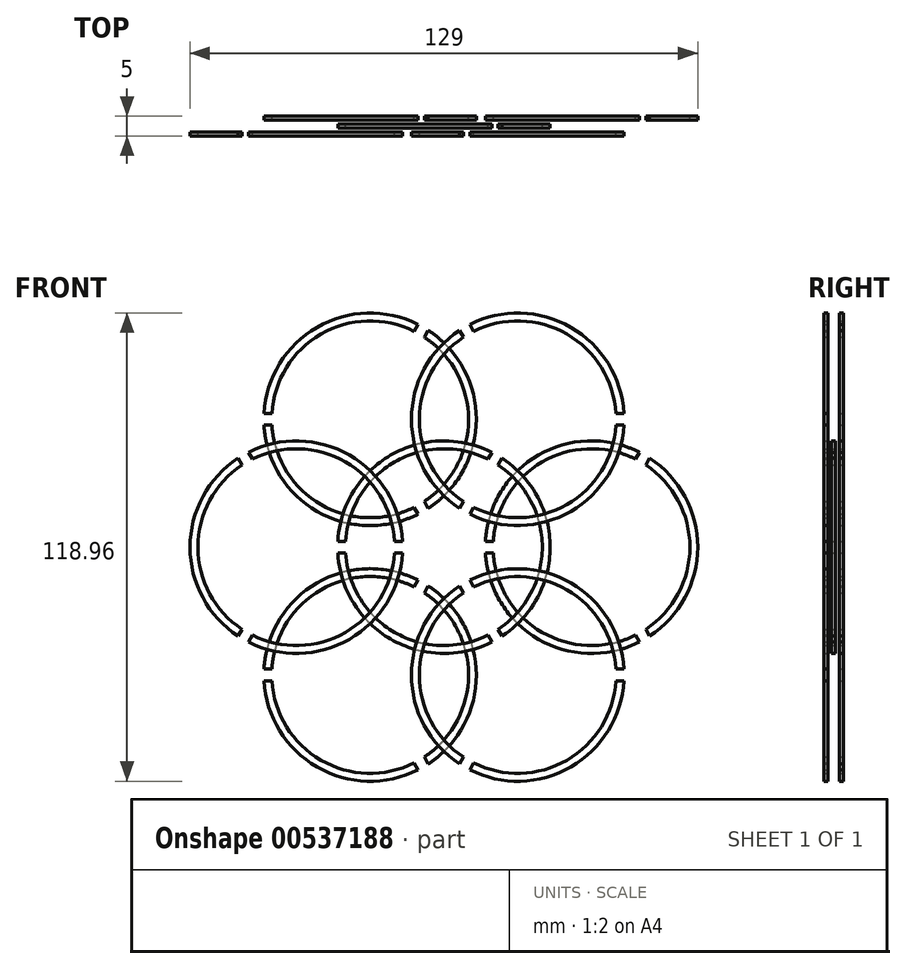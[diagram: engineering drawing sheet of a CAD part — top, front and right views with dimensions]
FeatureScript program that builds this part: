
annotation { "Feature Type Name" : "Feature", "Feature Type Description" : "" }
export const myFeature = defineFeature(function(context is Context, id is Id, definition is map)
    precondition{}
    {
        {
            var Q0;
            Q0=qCreatedBy(makeId("Front.planeOp"),FACE);
            var sketch = newSketch(context, id + "F0", { "sketchPlane" : qUnion([Q0])});
            skCircle(sketch, "E0", {"center": v(0, 0) * mm, "radius": 25 * mm});
            skCircle(sketch, "E1", {"center": v(0, 0) * mm, "radius": 27 * mm});
            skLineSegment(sketch, "E2", {"start": v(0, 0) * mm, "end": v(37.5, 0) * mm});
            skSolve(sketch);
        }
        {
            var Q0;
            Q0=qCreatedBy(makeId("Right.planeOp"),FACE);
            var sketch = newSketch(context, id + "F1", { "sketchPlane" : qUnion([Q0])});
            skLineSegment(sketch, "E3", {"start": v(-11.65, 0) * mm, "end": v(13.33, 0) * mm});
            skSolve(sketch);
        }
        {
            var Q0;
            Q0=makeQuery(id+"F0.imprint","IMPRINT",FACE,{"disambiguationData":[TD([[makeQuery(id+"F0.imprint","IMPRINT",EDGE,{"derivedFrom":sQuery(id+"F0.wireOp",EDGE,"E0")}),-1.0]])]});
            extrude(context, id + "F2", {"entities" : qUnion([Q0]), "depth" : 1 * mm, "offsetDistance" : 25 * mm});
        }
        {
            var Q0;
            Q0=qCreatedBy(makeId("Top.planeOp"),FACE);
            var sketch = newSketch(context, id + "F3", { "sketchPlane" : qUnion([Q0])});
            skLineSegment(sketch, "E4.bottom", {"start": v(16.08, -5.47) * mm, "end": v(-28.7, -5.47) * mm});
            skLineSegment(sketch, "E4.top", {"start": v(16.08, 4.96) * mm, "end": v(-28.7, 4.96) * mm});
            skLineSegment(sketch, "E4.left", {"start": v(16.08, -5.47) * mm, "end": v(16.08, 4.96) * mm});
            skLineSegment(sketch, "E4.right", {"start": v(-28.7, -5.47) * mm, "end": v(-28.7, 4.96) * mm});
            skSolve(sketch);
        }
        {
            var Q0;
            Q0=makeQuery(id+"F3.imprint","IMPRINT",FACE,{"disambiguationData":[TD([[makeQuery(id+"F3.imprint","IMPRINT",EDGE,{"derivedFrom":sQuery(id+"F3.wireOp",EDGE,"E4.bottom")}),-1.0]])]});
            extrude(context, id + "F4", {"entities" : qUnion([Q0]), "depth" : 3 * mm, "offsetDistance" : 25 * mm, "symmetric" : true});
        }
        {
            var Q0;
            Q0=makeQuery(id+"F4.opExtrude","SWEPT_BODY",BODY,{"disambiguationData":[OSD([sQuery(id+"F3.wireOp",EDGE,"E4.bottom"),sQuery(id+"F3.wireOp",EDGE,"E4.top"),sQuery(id+"F3.wireOp",EDGE,"E4.left"),sQuery(id+"F3.wireOp",EDGE,"E4.right")])]});
            var Q1;
            Q1=sQuery(id+"F1.wireOp",EDGE,"E3");
            circularPattern(context, id + "F5", {"entities" : qUnion([Q0]), "axis" : qUnion([Q1]), "angle" : 360 * degree, "instanceCount" : 3, "equalSpace" : true});
        }
        {
            var Q0;
            Q0=makeQuery(id+"F4.opExtrude","SWEPT_BODY",BODY,{"disambiguationData":[OSD([sQuery(id+"F3.wireOp",EDGE,"E4.bottom"),sQuery(id+"F3.wireOp",EDGE,"E4.top"),sQuery(id+"F3.wireOp",EDGE,"E4.left"),sQuery(id+"F3.wireOp",EDGE,"E4.right")])]});
            var Q1;
            Q1=makeQuery(id+"F5.opPattern","COPY",BODY,{"derivedFrom":makeQuery(id+"F4.opExtrude","SWEPT_BODY",BODY,{"disambiguationData":[OSD([sQuery(id+"F3.wireOp",EDGE,"E4.bottom"),sQuery(id+"F3.wireOp",EDGE,"E4.top"),sQuery(id+"F3.wireOp",EDGE,"E4.left"),sQuery(id+"F3.wireOp",EDGE,"E4.right")])]}),"instanceName":"2"});
            var Q2;
            Q2=makeQuery(id+"F5.opPattern","COPY",BODY,{"derivedFrom":makeQuery(id+"F4.opExtrude","SWEPT_BODY",BODY,{"disambiguationData":[OSD([sQuery(id+"F3.wireOp",EDGE,"E4.bottom"),sQuery(id+"F3.wireOp",EDGE,"E4.top"),sQuery(id+"F3.wireOp",EDGE,"E4.left"),sQuery(id+"F3.wireOp",EDGE,"E4.right")])]}),"instanceName":"1"});
            var Q3;
            Q3=makeQuery(id+"F2.opExtrude","SWEPT_BODY",BODY,{"disambiguationData":[OSD([sQuery(id+"F0.wireOp",EDGE,"E0"),sQuery(id+"F0.wireOp",EDGE,"E1")])]});
            var Q4;
            Q4=makeQuery(id+"F9.opPattern","COPY",BODY,{"derivedFrom":makeQuery(id+"F8.opPattern","COPY",BODY,{"derivedFrom":makeQuery(id+"F7.opPattern","COPY",BODY,{"derivedFrom":makeQuery(id+"F2.opExtrude","SWEPT_BODY",BODY,{"disambiguationData":[OSD([sQuery(id+"F0.wireOp",EDGE,"E0"),sQuery(id+"F0.wireOp",EDGE,"E1")])]}),"instanceName":"1"}),"instanceName":"1"}),"instanceName":"1"});
            var Q5;
            Q5=makeQuery(id+"F9.opPattern","COPY",BODY,{"derivedFrom":makeQuery(id+"F8.opPattern","COPY",BODY,{"derivedFrom":makeQuery(id+"F7.opPattern","COPY",BODY,{"derivedFrom":makeQuery(id+"F2.opExtrude","SWEPT_BODY",BODY,{"disambiguationData":[OSD([sQuery(id+"F0.wireOp",EDGE,"E0"),sQuery(id+"F0.wireOp",EDGE,"E1")])]}),"instanceName":"1"}),"instanceName":"2"}),"instanceName":"1"});
            var Q6;
            Q6=makeQuery(id+"F7.opPattern","COPY",BODY,{"derivedFrom":makeQuery(id+"F2.opExtrude","SWEPT_BODY",BODY,{"disambiguationData":[OSD([sQuery(id+"F0.wireOp",EDGE,"E0"),sQuery(id+"F0.wireOp",EDGE,"E1")])]}),"instanceName":"1"});
            var Q7;
            Q7=makeQuery(id+"F9.opPattern","COPY",BODY,{"derivedFrom":makeQuery(id+"F7.opPattern","COPY",BODY,{"derivedFrom":makeQuery(id+"F2.opExtrude","SWEPT_BODY",BODY,{"disambiguationData":[OSD([sQuery(id+"F0.wireOp",EDGE,"E0"),sQuery(id+"F0.wireOp",EDGE,"E1")])]}),"instanceName":"1"}),"instanceName":"1"});
            var Q8;
            Q8=makeQuery(id+"F8.opPattern","COPY",BODY,{"derivedFrom":makeQuery(id+"F7.opPattern","COPY",BODY,{"derivedFrom":makeQuery(id+"F2.opExtrude","SWEPT_BODY",BODY,{"disambiguationData":[OSD([sQuery(id+"F0.wireOp",EDGE,"E0"),sQuery(id+"F0.wireOp",EDGE,"E1")])]}),"instanceName":"1"}),"instanceName":"1"});
            var Q9;
            Q9=makeQuery(id+"F8.opPattern","COPY",BODY,{"derivedFrom":makeQuery(id+"F7.opPattern","COPY",BODY,{"derivedFrom":makeQuery(id+"F2.opExtrude","SWEPT_BODY",BODY,{"disambiguationData":[OSD([sQuery(id+"F0.wireOp",EDGE,"E0"),sQuery(id+"F0.wireOp",EDGE,"E1")])]}),"instanceName":"1"}),"instanceName":"2"});
            booleanBodies(context, id + "F6", {"operationType" : BooleanOperationType.SUBTRACTION, "tools" : qUnion([Q0, Q1, Q2]), "targets" : qUnion([Q3, Q4, Q5, Q6, Q7, Q8, Q9])});
        }
        {
            var Q0;
            Q0=makeQuery(id+"F2.opExtrude","SWEPT_BODY",BODY,{"disambiguationData":[OSD([sQuery(id+"F0.wireOp",EDGE,"E0"),sQuery(id+"F0.wireOp",EDGE,"E1")])]});
            transform(context, id + "F7", {"entities" : qUnion([Q0]), "transformType" : TransformType.TRANSLATION_3D, "dx" : 37.5 * mm, "dy" : 2 * mm, "dz" : 0 * mm, "makeCopy" : true});
        }
        {
            var Q0;
            Q0=makeQuery(id+"F7.opPattern","COPY",BODY,{"derivedFrom":makeQuery(id+"F2.opExtrude","SWEPT_BODY",BODY,{"disambiguationData":[OSD([sQuery(id+"F0.wireOp",EDGE,"E0"),sQuery(id+"F0.wireOp",EDGE,"E1")])]}),"instanceName":"1"});
            var Q1;
            Q1=sQuery(id+"F1.wireOp",EDGE,"E3");
            circularPattern(context, id + "F8", {"entities" : qUnion([Q0]), "axis" : qUnion([Q1]), "angle" : 360 * degree, "instanceCount" : 3, "equalSpace" : true});
        }
        {
            var Q0;
            Q0=makeQuery(id+"F8.opPattern","COPY",BODY,{"derivedFrom":makeQuery(id+"F7.opPattern","COPY",BODY,{"derivedFrom":makeQuery(id+"F2.opExtrude","SWEPT_BODY",BODY,{"disambiguationData":[OSD([sQuery(id+"F0.wireOp",EDGE,"E0"),sQuery(id+"F0.wireOp",EDGE,"E1")])]}),"instanceName":"1"}),"instanceName":"2"});
            var Q1;
            Q1=makeQuery(id+"F8.opPattern","COPY",BODY,{"derivedFrom":makeQuery(id+"F7.opPattern","COPY",BODY,{"derivedFrom":makeQuery(id+"F2.opExtrude","SWEPT_BODY",BODY,{"disambiguationData":[OSD([sQuery(id+"F0.wireOp",EDGE,"E0"),sQuery(id+"F0.wireOp",EDGE,"E1")])]}),"instanceName":"1"}),"instanceName":"1"});
            var Q2;
            Q2=makeQuery(id+"F7.opPattern","COPY",BODY,{"derivedFrom":makeQuery(id+"F2.opExtrude","SWEPT_BODY",BODY,{"disambiguationData":[OSD([sQuery(id+"F0.wireOp",EDGE,"E0"),sQuery(id+"F0.wireOp",EDGE,"E1")])]}),"instanceName":"1"});
            var Q3;
            Q3=sQuery(id+"F1.wireOp",EDGE,"E3");
            transform(context, id + "F9", {"entities" : qUnion([Q0, Q1, Q2]), "transformType" : TransformType.ROTATION, "transformAxis" : qUnion([Q3]), "angle" : 60 * degree, "makeCopy" : true});
        }
        {
            var Q0;
            Q0=makeQuery(id+"F9.opPattern","COPY",BODY,{"derivedFrom":makeQuery(id+"F7.opPattern","COPY",BODY,{"derivedFrom":makeQuery(id+"F2.opExtrude","SWEPT_BODY",BODY,{"disambiguationData":[OSD([sQuery(id+"F0.wireOp",EDGE,"E0"),sQuery(id+"F0.wireOp",EDGE,"E1")])]}),"instanceName":"1"}),"instanceName":"1"});
            var Q1;
            Q1=makeQuery(id+"F9.opPattern","COPY",BODY,{"derivedFrom":makeQuery(id+"F8.opPattern","COPY",BODY,{"derivedFrom":makeQuery(id+"F7.opPattern","COPY",BODY,{"derivedFrom":makeQuery(id+"F2.opExtrude","SWEPT_BODY",BODY,{"disambiguationData":[OSD([sQuery(id+"F0.wireOp",EDGE,"E0"),sQuery(id+"F0.wireOp",EDGE,"E1")])]}),"instanceName":"1"}),"instanceName":"2"}),"instanceName":"1"});
            var Q2;
            Q2=makeQuery(id+"F9.opPattern","COPY",BODY,{"derivedFrom":makeQuery(id+"F8.opPattern","COPY",BODY,{"derivedFrom":makeQuery(id+"F7.opPattern","COPY",BODY,{"derivedFrom":makeQuery(id+"F2.opExtrude","SWEPT_BODY",BODY,{"disambiguationData":[OSD([sQuery(id+"F0.wireOp",EDGE,"E0"),sQuery(id+"F0.wireOp",EDGE,"E1")])]}),"instanceName":"1"}),"instanceName":"1"}),"instanceName":"1"});
            transform(context, id + "F10", {"entities" : qUnion([Q0, Q1, Q2]), "transformType" : TransformType.TRANSLATION_3D, "dx" : 0 * mm, "dy" : -4 * mm, "dz" : 0 * mm, "makeCopy" : false});
        }
    });
